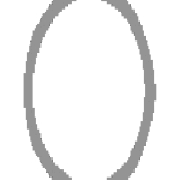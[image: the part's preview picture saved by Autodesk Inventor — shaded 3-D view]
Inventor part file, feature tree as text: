
AUTODESK INVENTOR PART (.ipt)
format: ipt  version: 2021 (Build 250183000, 183)  size: 112,128 bytes
history: native  units: in
note: dims shown in document units (in); Inventor stores cm internally (conversion verified against a paired STEP export)
features: other x4, sketch x3, plane x1
ambient origin geometry x8: Origin, YZ Plane, XZ Plane, XY Plane, X Axis, Y Axis, Z Axis, Center Point
bodies: Solid1 (feature_tree), Body (feature_tree)
feature tree (8):
  other  "Driven Length"
  other  "Frame Generator"
  other  "Start Plane"
  other  "End Plane"
  sketch  "Sketch"  dims[d2=12.431in d4=-0.0in d5=12.431in d6=0.12in d7=0.0in d8=90.0deg d9=12.431in]
  sketch  "Sketch2"  dims[d0=1.0in]
  plane  "Work Plane3"
  sketch  "Sketch3"  dims[d1=0.065in]
